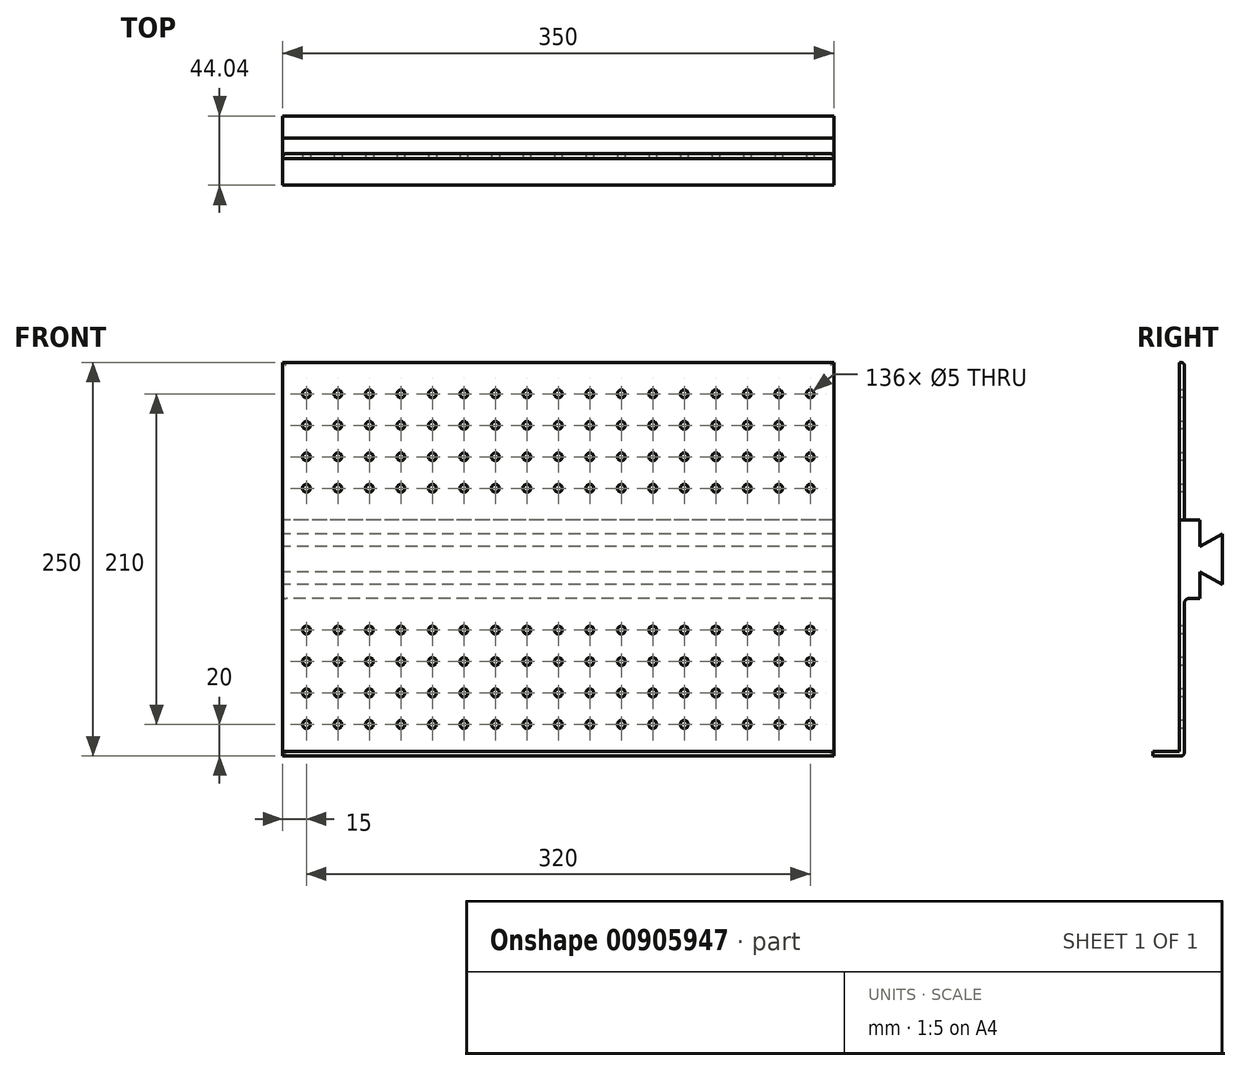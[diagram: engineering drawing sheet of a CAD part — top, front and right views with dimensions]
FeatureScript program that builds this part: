
annotation { "Feature Type Name" : "Feature", "Feature Type Description" : "" }
export const myFeature = defineFeature(function(context is Context, id is Id, definition is map)
    precondition{}
    {
        {
            var Q0;
            Q0=qCreatedBy(makeId("Front.planeOp"),FACE);
            var sketch = newSketch(context, id + "F0", { "sketchPlane" : qUnion([Q0])});
            skLineSegment(sketch, "E0.bottom", {"start": v(-175, 125) * mm, "end": v(175, 125) * mm});
            skLineSegment(sketch, "E0.top", {"start": v(-175, -125) * mm, "end": v(175, -125) * mm});
            skLineSegment(sketch, "E0.left", {"start": v(-175, 125) * mm, "end": v(-175, -125) * mm});
            skLineSegment(sketch, "E0.right", {"start": v(175, 125) * mm, "end": v(175, -125) * mm});
            skPoint(sketch, "E0.middle", {"position": v(0, 0) * mm});
            skSolve(sketch);
        }
        {
            var Q0;
            Q0 = qSketchRegion(id + "F0", true);
            extrude(context, id + "F1", {"entities" : qUnion([Q0]), "depth" : 20 * mm, "offsetDistance" : 25 * mm});
        }
        {
            var Q0;
            Q0=makeQuery(id+"F1.opExtrude","SWEPT_FACE",FACE,{"disambiguationData":[OSD([sQuery(id+"F0.wireOp",EDGE,"E0.right")])]});
            var sketch = newSketch(context, id + "F2", { "sketchPlane" : qUnion([Q0])});
            skLineSegment(sketch, "E1.bottom", {"start": v(-20, 125) * mm, "end": v(-3, 125) * mm});
            skLineSegment(sketch, "E1.top", {"start": v(-20, -122) * mm, "end": v(-3, -122) * mm});
            skLineSegment(sketch, "E1.left", {"start": v(-20, 125) * mm, "end": v(-20, -122) * mm});
            skLineSegment(sketch, "E1.right", {"start": v(-3, 125) * mm, "end": v(-3, -122) * mm});
            skSolve(sketch);
        }
        {
            var Q0;
            Q0 = qSketchRegion(id + "F2", true);
            extrude(context, id + "F3", {"entities" : qUnion([Q0]), "operationType" : NewBodyOperationType.REMOVE, "endBound" : BoundingType.UP_TO_NEXT, "oppositeDirection" : true, "depth" : 25 * mm, "offsetDistance" : 25 * mm});
        }
        {
            var Q0;
            Q0=qCreatedBy(makeId("Right.planeOp"),FACE);
            var sketch = newSketch(context, id + "F4", { "sketchPlane" : qUnion([Q0])});
            skLineSegment(sketch, "E2.bottom", {"start": v(0, 25) * mm, "end": v(10, 25) * mm});
            skLineSegment(sketch, "E2.top", {"start": v(0, -25) * mm, "end": v(10, -25) * mm});
            skLineSegment(sketch, "E2.left", {"start": v(0, 25) * mm, "end": v(0, -25) * mm});
            skLineSegment(sketch, "E2.right", {"start": v(10, 25) * mm, "end": v(10, 8) * mm});
            skLineSegment(sketch, "E3", {"start": v(10, 8) * mm, "end": v(24.04, 16.1) * mm});
            skLineSegment(sketch, "E4", {"start": v(24.04, 16.1) * mm, "end": v(24.04, -16.1) * mm});
            skLineSegment(sketch, "E5", {"start": v(24.04, -16.1) * mm, "end": v(10, -8) * mm});
            skLineSegment(sketch, "E6.trimOffspring", {"start": v(10, -8) * mm, "end": v(10, -25) * mm});
            skLineSegment(sketch, "E7", {"start": v(0, 0) * mm, "end": v(24.04, 0) * mm, "construction": true});
            skSolve(sketch);
        }
        {
            var Q0;
            Q0 = qSketchRegion(id + "F4", true);
            extrude(context, id + "F5", {"entities" : qUnion([Q0]), "operationType" : NewBodyOperationType.ADD, "endBound" : BoundingType.SYMMETRIC, "depth" : 350 * mm, "offsetDistance" : 25 * mm});
        }
        {
            var Q0;
            Q0=makeQuery(id+"F5.opExtrude","SWEPT_EDGE",EDGE,{"disambiguationData":[OSD([sQuery(id+"F4.wireOp",EDGE,"E2.bottom"),sQuery(id+"F4.wireOp",EDGE,"E2.left")])]});
            var Q1;
            Q1=makeQuery(id+"F5.opExtrude","SWEPT_EDGE",EDGE,{"disambiguationData":[OSD([sQuery(id+"F4.wireOp",EDGE,"E2.top"),sQuery(id+"F4.wireOp",EDGE,"E2.left")])]});
            fillet(context, id + "F6", {"entities" : qUnion([Q0, Q1]), "radius" : 3 * mm, "tangentPropagation" : true, "allowEdgeOverflow" : false});
        }
        {
            var Q0;
            {var subQ1=sQuery(id+"F0.wireOp",EDGE,"E0.left");var subQ2=sQuery(id+"F0.wireOp",EDGE,"E0.top");Q0=makeQuery(id+"F5.boolean.opBoolean","SPLIT",EDGE,{"disambiguationData":[TD([makeQuery(id+"F1.opExtrude","SWEPT_FACE",FACE,{"disambiguationData":[OSD([subQ2])]})])],"derivedFrom":makeQuery(id+"F1.opExtrude","CAP_EDGE",EDGE,{"disambiguationData":[OSD([subQ1])],"isStart":true})});}
            var Q1;
            {var subQ1=sQuery(id+"F0.wireOp",EDGE,"E0.left");var subQ2=sQuery(id+"F0.wireOp",EDGE,"E0.bottom");Q1=makeQuery(id+"F5.boolean.opBoolean","SPLIT",EDGE,{"disambiguationData":[TD([makeQuery(id+"F1.opExtrude","SWEPT_FACE",FACE,{"disambiguationData":[OSD([subQ2])]})])],"derivedFrom":makeQuery(id+"F1.opExtrude","CAP_EDGE",EDGE,{"disambiguationData":[OSD([subQ1])],"isStart":true})});}
            var Q2;
            {var subQ1=sQuery(id+"F0.wireOp",EDGE,"E0.right");var subQ2=sQuery(id+"F0.wireOp",EDGE,"E0.bottom");Q2=makeQuery(id+"F5.boolean.opBoolean","SPLIT",EDGE,{"disambiguationData":[TD([makeQuery(id+"F1.opExtrude","SWEPT_FACE",FACE,{"disambiguationData":[OSD([subQ2])]})])],"derivedFrom":makeQuery(id+"F1.opExtrude","CAP_EDGE",EDGE,{"disambiguationData":[OSD([subQ1])],"isStart":true})});}
            var Q3;
            {var subQ1=sQuery(id+"F0.wireOp",EDGE,"E0.right");var subQ2=sQuery(id+"F0.wireOp",EDGE,"E0.top");Q3=makeQuery(id+"F5.boolean.opBoolean","SPLIT",EDGE,{"disambiguationData":[TD([makeQuery(id+"F1.opExtrude","SWEPT_FACE",FACE,{"disambiguationData":[OSD([subQ2])]})])],"derivedFrom":makeQuery(id+"F1.opExtrude","CAP_EDGE",EDGE,{"disambiguationData":[OSD([subQ1])],"isStart":true})});}
            var Q4;
            Q4=makeQuery(id+"F1.opExtrude","CAP_EDGE",EDGE,{"disambiguationData":[OSD([sQuery(id+"F0.wireOp",EDGE,"E0.top")])],"isStart":true});
            var Q5;
            Q5=makeQuery(id+"F1.opExtrude","CAP_EDGE",EDGE,{"disambiguationData":[OSD([sQuery(id+"F0.wireOp",EDGE,"E0.bottom")])],"isStart":true});
            fillet(context, id + "F7", {"entities" : qUnion([Q0, Q1, Q2, Q3, Q4, Q5]), "radius" : 2 * mm, "tangentPropagation" : true, "allowEdgeOverflow" : false});
        }
        {
            var Q0;
            Q0=makeQuery(id+"F3.boolean.opBoolean","COPY",FACE,{"derivedFrom":makeQuery(id+"F3.opExtrude","SWEPT_FACE",FACE,{"disambiguationData":[OSD([sQuery(id+"F2.wireOp",EDGE,"E1.right")])]})});
            var sketch = newSketch(context, id + "F8", { "sketchPlane" : qUnion([Q0])});
            skCircle(sketch, "E8", {"center": v(-160, 105) * mm, "radius": 2.5 * mm});
            skCircle(sketch, "E9", {"center": v(-160, 85) * mm, "radius": 2.5 * mm});
            skCircle(sketch, "E10", {"center": v(-160, 65) * mm, "radius": 2.5 * mm});
            skCircle(sketch, "E11", {"center": v(-160, 45) * mm, "radius": 2.5 * mm});
            skCircle(sketch, "E12.1.0.0", {"center": v(-140, 45) * mm, "radius": 2.5 * mm});
            skCircle(sketch, "E12.1.0.1", {"center": v(-140, 65) * mm, "radius": 2.5 * mm});
            skCircle(sketch, "E12.1.0.2", {"center": v(-140, 105) * mm, "radius": 2.5 * mm});
            skCircle(sketch, "E12.1.0.3", {"center": v(-140, 85) * mm, "radius": 2.5 * mm});
            skCircle(sketch, "E12.2.0.0", {"center": v(-120, 45) * mm, "radius": 2.5 * mm});
            skCircle(sketch, "E12.2.0.1", {"center": v(-120, 65) * mm, "radius": 2.5 * mm});
            skCircle(sketch, "E12.2.0.2", {"center": v(-120, 105) * mm, "radius": 2.5 * mm});
            skCircle(sketch, "E12.2.0.3", {"center": v(-120, 85) * mm, "radius": 2.5 * mm});
            skCircle(sketch, "E12.3.0.0", {"center": v(-100, 45) * mm, "radius": 2.5 * mm});
            skCircle(sketch, "E12.3.0.1", {"center": v(-100, 65) * mm, "radius": 2.5 * mm});
            skCircle(sketch, "E12.3.0.2", {"center": v(-100, 105) * mm, "radius": 2.5 * mm});
            skCircle(sketch, "E12.3.0.3", {"center": v(-100, 85) * mm, "radius": 2.5 * mm});
            skCircle(sketch, "E12.4.0.0", {"center": v(-80, 45) * mm, "radius": 2.5 * mm});
            skCircle(sketch, "E12.4.0.1", {"center": v(-80, 65) * mm, "radius": 2.5 * mm});
            skCircle(sketch, "E12.4.0.2", {"center": v(-80, 105) * mm, "radius": 2.5 * mm});
            skCircle(sketch, "E12.4.0.3", {"center": v(-80, 85) * mm, "radius": 2.5 * mm});
            skCircle(sketch, "E12.5.0.0", {"center": v(-60, 45) * mm, "radius": 2.5 * mm});
            skCircle(sketch, "E12.5.0.1", {"center": v(-60, 65) * mm, "radius": 2.5 * mm});
            skCircle(sketch, "E12.5.0.2", {"center": v(-60, 105) * mm, "radius": 2.5 * mm});
            skCircle(sketch, "E12.5.0.3", {"center": v(-60, 85) * mm, "radius": 2.5 * mm});
            skCircle(sketch, "E12.6.0.0", {"center": v(-40, 45) * mm, "radius": 2.5 * mm});
            skCircle(sketch, "E12.6.0.1", {"center": v(-40, 65) * mm, "radius": 2.5 * mm});
            skCircle(sketch, "E12.6.0.2", {"center": v(-40, 105) * mm, "radius": 2.5 * mm});
            skCircle(sketch, "E12.6.0.3", {"center": v(-40, 85) * mm, "radius": 2.5 * mm});
            skCircle(sketch, "E12.7.0.0", {"center": v(-20, 45) * mm, "radius": 2.5 * mm});
            skCircle(sketch, "E12.7.0.1", {"center": v(-20, 65) * mm, "radius": 2.5 * mm});
            skCircle(sketch, "E12.7.0.2", {"center": v(-20, 105) * mm, "radius": 2.5 * mm});
            skCircle(sketch, "E12.7.0.3", {"center": v(-20, 85) * mm, "radius": 2.5 * mm});
            skCircle(sketch, "E12.8.0.0", {"center": v(0, 45) * mm, "radius": 2.5 * mm});
            skCircle(sketch, "E12.8.0.1", {"center": v(0, 65) * mm, "radius": 2.5 * mm});
            skCircle(sketch, "E12.8.0.2", {"center": v(0, 105) * mm, "radius": 2.5 * mm});
            skCircle(sketch, "E12.8.0.3", {"center": v(0, 85) * mm, "radius": 2.5 * mm});
            skCircle(sketch, "E12.9.0.0", {"center": v(20, 45) * mm, "radius": 2.5 * mm});
            skCircle(sketch, "E12.9.0.1", {"center": v(20, 65) * mm, "radius": 2.5 * mm});
            skCircle(sketch, "E12.9.0.2", {"center": v(20, 105) * mm, "radius": 2.5 * mm});
            skCircle(sketch, "E12.9.0.3", {"center": v(20, 85) * mm, "radius": 2.5 * mm});
            skCircle(sketch, "E12.10.0.0", {"center": v(40, 45) * mm, "radius": 2.5 * mm});
            skCircle(sketch, "E12.10.0.1", {"center": v(40, 65) * mm, "radius": 2.5 * mm});
            skCircle(sketch, "E12.10.0.2", {"center": v(40, 105) * mm, "radius": 2.5 * mm});
            skCircle(sketch, "E12.10.0.3", {"center": v(40, 85) * mm, "radius": 2.5 * mm});
            skCircle(sketch, "E12.11.0.0", {"center": v(60, 45) * mm, "radius": 2.5 * mm});
            skCircle(sketch, "E12.11.0.1", {"center": v(60, 65) * mm, "radius": 2.5 * mm});
            skCircle(sketch, "E12.11.0.2", {"center": v(60, 105) * mm, "radius": 2.5 * mm});
            skCircle(sketch, "E12.11.0.3", {"center": v(60, 85) * mm, "radius": 2.5 * mm});
            skCircle(sketch, "E12.12.0.0", {"center": v(80, 45) * mm, "radius": 2.5 * mm});
            skCircle(sketch, "E12.12.0.1", {"center": v(80, 65) * mm, "radius": 2.5 * mm});
            skCircle(sketch, "E12.12.0.2", {"center": v(80, 105) * mm, "radius": 2.5 * mm});
            skCircle(sketch, "E12.12.0.3", {"center": v(80, 85) * mm, "radius": 2.5 * mm});
            skCircle(sketch, "E12.13.0.0", {"center": v(100, 45) * mm, "radius": 2.5 * mm});
            skCircle(sketch, "E12.13.0.1", {"center": v(100, 65) * mm, "radius": 2.5 * mm});
            skCircle(sketch, "E12.13.0.2", {"center": v(100, 105) * mm, "radius": 2.5 * mm});
            skCircle(sketch, "E12.13.0.3", {"center": v(100, 85) * mm, "radius": 2.5 * mm});
            skCircle(sketch, "E12.14.0.0", {"center": v(120, 45) * mm, "radius": 2.5 * mm});
            skCircle(sketch, "E12.14.0.1", {"center": v(120, 65) * mm, "radius": 2.5 * mm});
            skCircle(sketch, "E12.14.0.2", {"center": v(120, 105) * mm, "radius": 2.5 * mm});
            skCircle(sketch, "E12.14.0.3", {"center": v(120, 85) * mm, "radius": 2.5 * mm});
            skCircle(sketch, "E12.15.0.0", {"center": v(140, 45) * mm, "radius": 2.5 * mm});
            skCircle(sketch, "E12.15.0.1", {"center": v(140, 65) * mm, "radius": 2.5 * mm});
            skCircle(sketch, "E12.15.0.2", {"center": v(140, 105) * mm, "radius": 2.5 * mm});
            skCircle(sketch, "E12.15.0.3", {"center": v(140, 85) * mm, "radius": 2.5 * mm});
            skCircle(sketch, "E12.16.0.0", {"center": v(160, 45) * mm, "radius": 2.5 * mm});
            skCircle(sketch, "E12.16.0.1", {"center": v(160, 65) * mm, "radius": 2.5 * mm});
            skCircle(sketch, "E12.16.0.2", {"center": v(160, 105) * mm, "radius": 2.5 * mm});
            skCircle(sketch, "E12.16.0.3", {"center": v(160, 85) * mm, "radius": 2.5 * mm});
            skLineSegment(sketch, "E12.direction1", {"start": v(-160, 45) * mm, "end": v(-140, 45) * mm, "construction": true});
            skCircle(sketch, "E13.MirrorC", {"center": v(-140, -45) * mm, "radius": 2.5 * mm});
            skCircle(sketch, "E14.MirrorC", {"center": v(-160, -45) * mm, "radius": 2.5 * mm});
            skCircle(sketch, "E15.MirrorC", {"center": v(-120, -45) * mm, "radius": 2.5 * mm});
            skCircle(sketch, "E16.MirrorC", {"center": v(20, -85) * mm, "radius": 2.5 * mm});
            skCircle(sketch, "E17.MirrorC", {"center": v(120, -45) * mm, "radius": 2.5 * mm});
            skCircle(sketch, "E18.MirrorC", {"center": v(40, -45) * mm, "radius": 2.5 * mm});
            skCircle(sketch, "E19.MirrorC", {"center": v(-40, -45) * mm, "radius": 2.5 * mm});
            skCircle(sketch, "E20.MirrorC", {"center": v(-140, -85) * mm, "radius": 2.5 * mm});
            skCircle(sketch, "E21.MirrorC", {"center": v(100, -85) * mm, "radius": 2.5 * mm});
            skCircle(sketch, "E22.MirrorC", {"center": v(80, -85) * mm, "radius": 2.5 * mm});
            skCircle(sketch, "E23.MirrorC", {"center": v(0, -85) * mm, "radius": 2.5 * mm});
            skCircle(sketch, "E24.MirrorC", {"center": v(-120, -85) * mm, "radius": 2.5 * mm});
            skCircle(sketch, "E25.MirrorC", {"center": v(-80, -85) * mm, "radius": 2.5 * mm});
            skCircle(sketch, "E26.MirrorC", {"center": v(160, -85) * mm, "radius": 2.5 * mm});
            skCircle(sketch, "E27.MirrorC", {"center": v(-140, -105) * mm, "radius": 2.5 * mm});
            skCircle(sketch, "E28.MirrorC", {"center": v(-140, -65) * mm, "radius": 2.5 * mm});
            skCircle(sketch, "E29.MirrorC", {"center": v(-100, -45) * mm, "radius": 2.5 * mm});
            skCircle(sketch, "E30.MirrorC", {"center": v(140, -45) * mm, "radius": 2.5 * mm});
            skCircle(sketch, "E31.MirrorC", {"center": v(100, -65) * mm, "radius": 2.5 * mm});
            skCircle(sketch, "E32.MirrorC", {"center": v(60, -45) * mm, "radius": 2.5 * mm});
            skCircle(sketch, "E33.MirrorC", {"center": v(20, -65) * mm, "radius": 2.5 * mm});
            skCircle(sketch, "E34.MirrorC", {"center": v(-20, -45) * mm, "radius": 2.5 * mm});
            skCircle(sketch, "E35.MirrorC", {"center": v(-60, -65) * mm, "radius": 2.5 * mm});
            skCircle(sketch, "E36.MirrorC", {"center": v(60, -105) * mm, "radius": 2.5 * mm});
            skCircle(sketch, "E37.MirrorC", {"center": v(-20, -105) * mm, "radius": 2.5 * mm});
            skCircle(sketch, "E38.MirrorC", {"center": v(160, -105) * mm, "radius": 2.5 * mm});
            skCircle(sketch, "E39.MirrorC", {"center": v(-60, -45) * mm, "radius": 2.5 * mm});
            skCircle(sketch, "E40.MirrorC", {"center": v(-100, -85) * mm, "radius": 2.5 * mm});
            skCircle(sketch, "E41.MirrorC", {"center": v(-120, -65) * mm, "radius": 2.5 * mm});
            skCircle(sketch, "E42.MirrorC", {"center": v(140, -105) * mm, "radius": 2.5 * mm});
            skCircle(sketch, "E43.MirrorC", {"center": v(-40, -65) * mm, "radius": 2.5 * mm});
            skCircle(sketch, "E44.MirrorC", {"center": v(0, -45) * mm, "radius": 2.5 * mm});
            skCircle(sketch, "E45.MirrorC", {"center": v(20, -45) * mm, "radius": 2.5 * mm});
            skCircle(sketch, "E46.MirrorC", {"center": v(80, -65) * mm, "radius": 2.5 * mm});
            skCircle(sketch, "E47.MirrorC", {"center": v(120, -65) * mm, "radius": 2.5 * mm});
            skCircle(sketch, "E48.MirrorC", {"center": v(100, -105) * mm, "radius": 2.5 * mm});
            skCircle(sketch, "E49.MirrorC", {"center": v(-160, -105) * mm, "radius": 2.5 * mm});
            skCircle(sketch, "E50.MirrorC", {"center": v(-60, -105) * mm, "radius": 2.5 * mm});
            skCircle(sketch, "E51.MirrorC", {"center": v(40, -65) * mm, "radius": 2.5 * mm});
            skCircle(sketch, "E52.MirrorC", {"center": v(0, -65) * mm, "radius": 2.5 * mm});
            skCircle(sketch, "E53.MirrorC", {"center": v(-40, -85) * mm, "radius": 2.5 * mm});
            skCircle(sketch, "E54.MirrorC", {"center": v(60, -65) * mm, "radius": 2.5 * mm});
            skCircle(sketch, "E55.MirrorC", {"center": v(-120, -105) * mm, "radius": 2.5 * mm});
            skCircle(sketch, "E56.MirrorC", {"center": v(40, -85) * mm, "radius": 2.5 * mm});
            skCircle(sketch, "E57.MirrorC", {"center": v(0, -105) * mm, "radius": 2.5 * mm});
            skCircle(sketch, "E58.MirrorC", {"center": v(80, -45) * mm, "radius": 2.5 * mm});
            skCircle(sketch, "E59.MirrorC", {"center": v(140, -65) * mm, "radius": 2.5 * mm});
            skCircle(sketch, "E60.MirrorC", {"center": v(-40, -105) * mm, "radius": 2.5 * mm});
            skCircle(sketch, "E61.MirrorC", {"center": v(-160, -65) * mm, "radius": 2.5 * mm});
            skCircle(sketch, "E62.MirrorC", {"center": v(-100, -105) * mm, "radius": 2.5 * mm});
            skCircle(sketch, "E63.MirrorC", {"center": v(160, -65) * mm, "radius": 2.5 * mm});
            skCircle(sketch, "E64.MirrorC", {"center": v(-80, -65) * mm, "radius": 2.5 * mm});
            skCircle(sketch, "E65.MirrorC", {"center": v(100, -45) * mm, "radius": 2.5 * mm});
            skCircle(sketch, "E66.MirrorC", {"center": v(-20, -85) * mm, "radius": 2.5 * mm});
            skCircle(sketch, "E67.MirrorC", {"center": v(-80, -45) * mm, "radius": 2.5 * mm});
            skCircle(sketch, "E68.MirrorC", {"center": v(-20, -65) * mm, "radius": 2.5 * mm});
            skCircle(sketch, "E69.MirrorC", {"center": v(-100, -65) * mm, "radius": 2.5 * mm});
            skCircle(sketch, "E70.MirrorC", {"center": v(120, -105) * mm, "radius": 2.5 * mm});
            skCircle(sketch, "E71.MirrorC", {"center": v(-160, -85) * mm, "radius": 2.5 * mm});
            skCircle(sketch, "E72.MirrorC", {"center": v(80, -105) * mm, "radius": 2.5 * mm});
            skCircle(sketch, "E73.MirrorC", {"center": v(60, -85) * mm, "radius": 2.5 * mm});
            skCircle(sketch, "E74.MirrorC", {"center": v(120, -85) * mm, "radius": 2.5 * mm});
            skCircle(sketch, "E75.MirrorC", {"center": v(-60, -85) * mm, "radius": 2.5 * mm});
            skCircle(sketch, "E76.MirrorC", {"center": v(160, -45) * mm, "radius": 2.5 * mm});
            skCircle(sketch, "E77.MirrorC", {"center": v(20, -105) * mm, "radius": 2.5 * mm});
            skCircle(sketch, "E78.MirrorC", {"center": v(-80, -105) * mm, "radius": 2.5 * mm});
            skCircle(sketch, "E79.MirrorC", {"center": v(140, -85) * mm, "radius": 2.5 * mm});
            skCircle(sketch, "E80.MirrorC", {"center": v(40, -105) * mm, "radius": 2.5 * mm});
            skSolve(sketch);
        }
        {
            var Q0;
            Q0 = qSketchRegion(id + "F8", true);
            extrude(context, id + "F9", {"entities" : qUnion([Q0]), "operationType" : NewBodyOperationType.REMOVE, "endBound" : BoundingType.UP_TO_NEXT, "oppositeDirection" : true, "depth" : 25 * mm, "offsetDistance" : 25 * mm});
        }
    });
